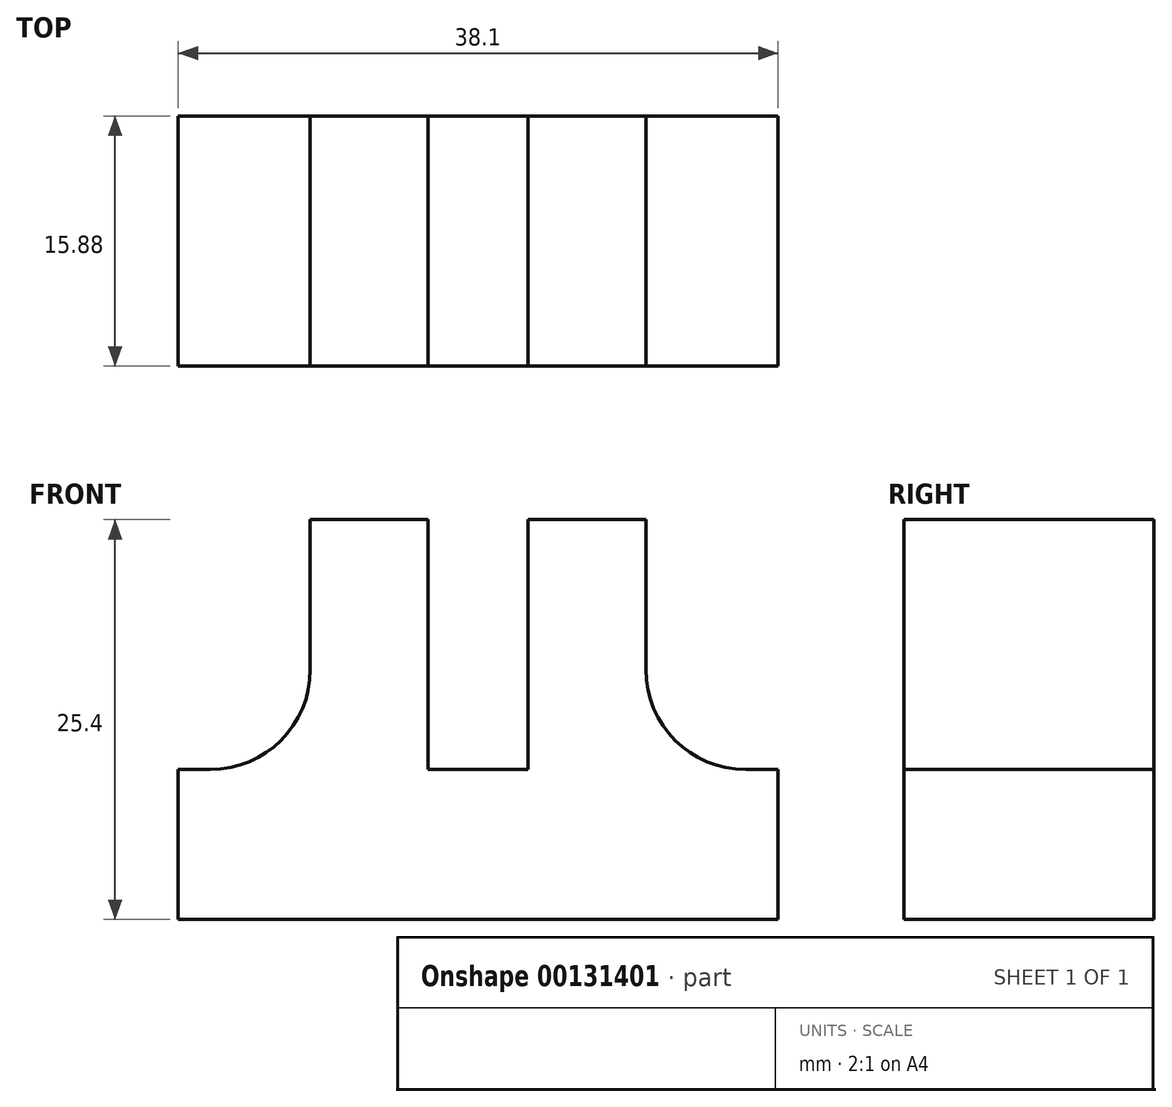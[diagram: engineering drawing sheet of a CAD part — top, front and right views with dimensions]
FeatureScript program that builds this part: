
annotation { "Feature Type Name" : "Feature", "Feature Type Description" : "" }
export const myFeature = defineFeature(function(context is Context, id is Id, definition is map)
    precondition{}
    {
        {
            var Q0;
            Q0=qCreatedBy(makeId("Front.planeOp"),FACE);
            var sketch = newSketch(context, id + "F0", { "sketchPlane" : qUnion([Q0])});
            skLineSegment(sketch, "E0.bottom", {"start": v(-19.05, 4.76) * mm, "end": v(-17, 4.76) * mm});
            skLineSegment(sketch, "E0.top", {"start": v(-19.05, -4.76) * mm, "end": v(19.05, -4.76) * mm});
            skLineSegment(sketch, "E0.left", {"start": v(-19.05, 4.76) * mm, "end": v(-19.05, -4.76) * mm});
            skLineSegment(sketch, "E0.right", {"start": v(19.05, 4.76) * mm, "end": v(19.05, -4.76) * mm});
            skPoint(sketch, "E0.middle", {"position": v(0, 0) * mm});
            skLineSegment(sketch, "E1.top", {"start": v(10.66, 20.64) * mm, "end": v(3.17, 20.64) * mm});
            skLineSegment(sketch, "E1.left", {"start": v(10.66, 11.11) * mm, "end": v(10.66, 20.64) * mm});
            skLineSegment(sketch, "E1.right", {"start": v(-10.66, 11.11) * mm, "end": v(-10.66, 20.64) * mm});
            skPoint(sketch, "E1.middle", {"position": v(0, 12.7) * mm});
            skLineSegment(sketch, "E2.bottom", {"start": v(3.18, 4.76) * mm, "end": v(-3.17, 4.76) * mm});
            skLineSegment(sketch, "E2.left", {"start": v(3.18, 4.76) * mm, "end": v(3.17, 20.64) * mm});
            skLineSegment(sketch, "E2.right", {"start": v(-3.17, 4.76) * mm, "end": v(-3.18, 20.64) * mm});
            skLineSegment(sketch, "E3.trimOffspring", {"start": v(-3.18, 20.64) * mm, "end": v(-10.66, 20.64) * mm});
            skPoint(sketch, "E4.newPointB", {"position": v(19.05, 4.76) * mm});
            skArc(sketch, "E4.filletArc", {"start": v(-17, 4.76) * mm, "mid": v(-12.52, 6.62) * mm, "end": v(-10.66, 11.11) * mm});
            skLineSegment(sketch, "E5", {"start": v(17, 4.76) * mm, "end": v(19.05, 4.76) * mm});
            skPoint(sketch, "E6.visualSharp", {"position": v(10.66, 4.76) * mm});
            skArc(sketch, "E6.filletArc", {"start": v(10.66, 11.11) * mm, "mid": v(12.52, 6.62) * mm, "end": v(17, 4.76) * mm});
            skPoint(sketch, "E1.bottom.end.orphan", {"position": v(-10.66, 4.76) * mm});
            skSolve(sketch);
        }
        {
            var Q0;
            Q0 = qSketchRegion(id + "F0", true);
            extrude(context, id + "F1", {"entities" : qUnion([Q0]), "depth" : 15.88 * mm});
        }
    });
